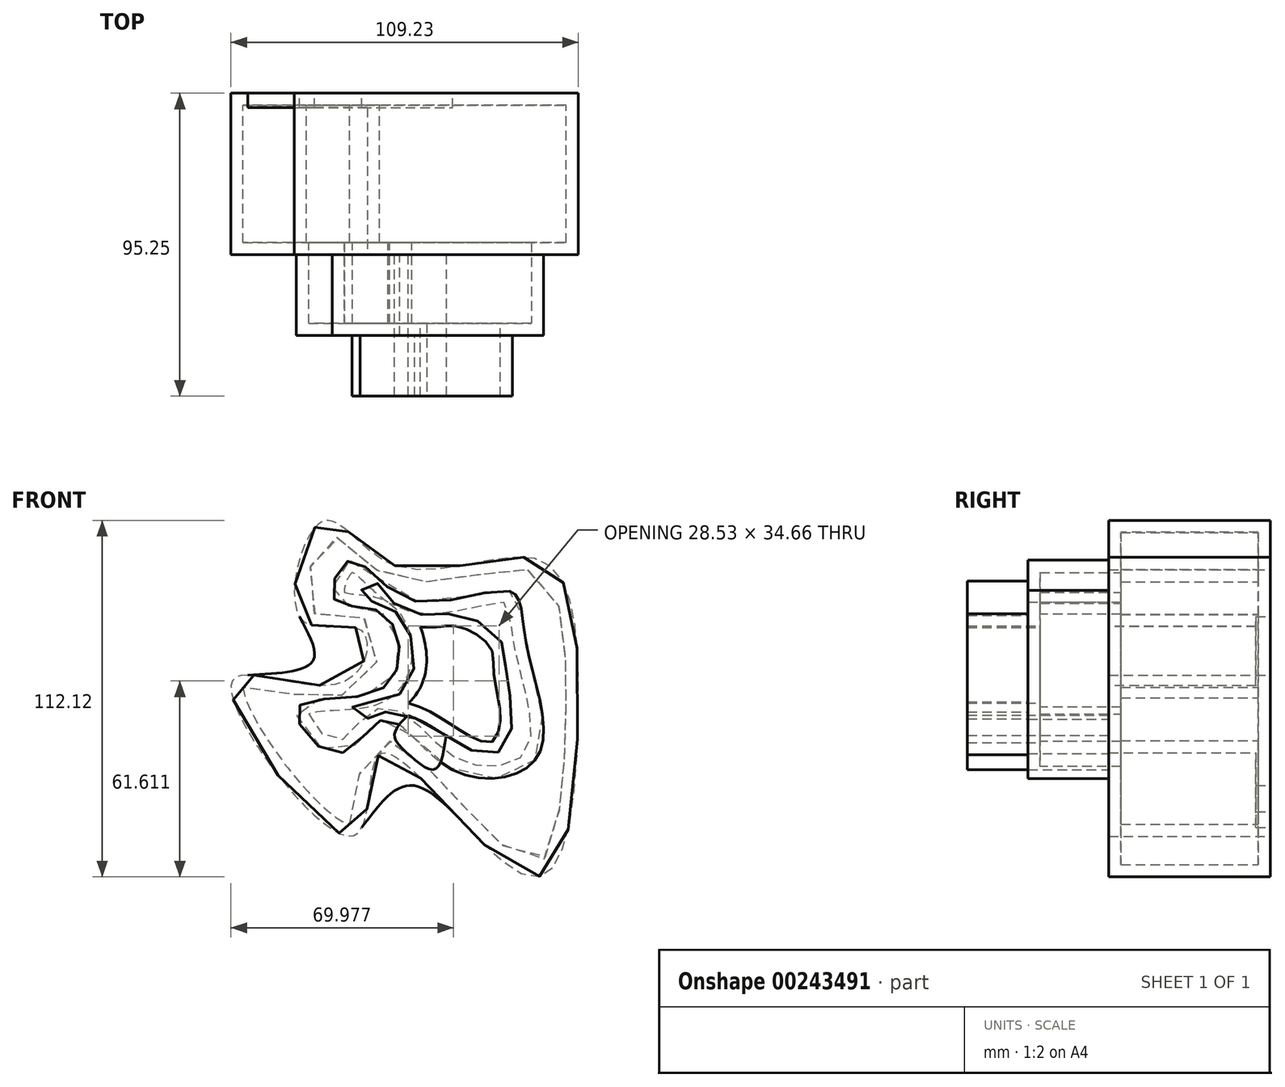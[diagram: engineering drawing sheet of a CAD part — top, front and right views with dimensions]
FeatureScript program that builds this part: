
annotation { "Feature Type Name" : "Feature", "Feature Type Description" : "" }
export const myFeature = defineFeature(function(context is Context, id is Id, definition is map)
    precondition{}
    {
        {
            var Q0;
            Q0=qCreatedBy(makeId("Front.planeOp"),FACE);
            var sketch = newSketch(context, id + "F0", { "sketchPlane" : qUnion([Q0])});
            skFitSpline(sketch, "E0", {"points": [v(-12.4, 45.2) * mm, v(-35.36, 59.05) * mm, v(-41.92, 28.43) * mm, v(-22.97, 24.79) * mm, v(-29.16, 8.38) * mm, v(-63.8, 8.38) * mm, v(-25.52, -39.73) * mm, v(-16.77, -13.85) * mm, v(29.9, -52.5) * mm, v(45.2, 0) * mm, v(32.8, 47.02) * mm, v(-12.4, 45.2) * mm]});
            skSolve(sketch);
        }
        {
            var Q0;
            Q0=makeQuery(id+"F0.imprint","IMPRINT",FACE,{"disambiguationData":[TD([[makeQuery(id+"F0.imprint","IMPRINT",EDGE,{"derivedFrom":sQuery(id+"F0.wireOp",EDGE,"E0")}),1.0]])]});
            extrude(context, id + "F1", {"entities" : qUnion([Q0]), "depth" : 50.8 * mm});
        }
        {
            var Q0;
            Q0=makeQuery(id+"F1.opExtrude","CAP_FACE",FACE,{"disambiguationData":[OSD([sQuery(id+"F0.wireOp",EDGE,"E0")])],"isStart":false});
            var sketch = newSketch(context, id + "F2", { "sketchPlane" : qUnion([Q0])});
            skFitSpline(sketch, "E1", {"points": [v(23.64, 37.21) * mm, v(-7.87, 34.52) * mm, v(-26.7, 46.82) * mm, v(-31.7, 34.9) * mm, v(-17.86, 31.06) * mm, v(-10.94, 17.61) * mm, v(-19.78, 4.93) * mm, v(-43.22, 0) * mm, v(-30.54, -13.9) * mm, v(-15.94, -3.14) * mm, v(5.58, -18.9) * mm, v(32.48, -14.67) * mm, v(28.64, 21.84) * mm, v(23.64, 37.21) * mm]});
            skSolve(sketch);
        }
        {
            var Q0;
            Q0=makeQuery(id+"F2.imprint","IMPRINT",FACE,{"disambiguationData":[TD([[makeQuery(id+"F2.imprint","IMPRINT",EDGE,{"derivedFrom":sQuery(id+"F2.wireOp",EDGE,"E1")}),1.0]])]});
            extrude(context, id + "F3", {"entities" : qUnion([Q0]), "operationType" : NewBodyOperationType.ADD, "depth" : 25.4 * mm});
        }
        {
            var Q0;
            Q0=makeQuery(id+"F3.opExtrude","CAP_FACE",FACE,{"disambiguationData":[OSD([sQuery(id+"F2.wireOp",EDGE,"E1")])],"isStart":false});
            var sketch = newSketch(context, id + "F4", { "sketchPlane" : qUnion([Q0])});
            skFitSpline(sketch, "E2", {"points": [v(21.07, 21.18) * mm, v(8.2, 29.82) * mm, v(-2.99, 29.65) * mm, v(-14.68, 35.24) * mm, v(-19.6, 40.33) * mm, v(-23.32, 35.92) * mm, v(-16.71, 33.2) * mm, v(-8.92, 26.6) * mm, v(-6.89, 11) * mm, v(-16.04, 2.54) * mm, v(-25.86, 1.52) * mm, v(-21.97, -2.89) * mm, v(-18.75, -1.36) * mm, v(-7.05, -2.38) * mm, v(6.67, -10.17) * mm, v(19.21, -13.9) * mm, v(24.46, -3.73) * mm, v(22.43, 11.86) * mm, v(21.07, 21.18) * mm]});
            skSolve(sketch);
        }
        {
            var Q0;
            Q0=makeQuery(id+"F4.imprint","IMPRINT",FACE,{"disambiguationData":[TD([[makeQuery(id+"F4.imprint","IMPRINT",EDGE,{"derivedFrom":sQuery(id+"F4.wireOp",EDGE,"E2")}),1.0]])]});
            extrude(context, id + "F5", {"entities" : qUnion([Q0]), "operationType" : NewBodyOperationType.ADD, "depth" : 19.05 * mm});
        }
        {
            var Q0;
            Q0=makeQuery(id+"F5.opExtrude","CAP_FACE",FACE,{"disambiguationData":[OSD([sQuery(id+"F4.wireOp",EDGE,"E2")])],"isStart":false});
            var sketch = newSketch(context, id + "F6", { "sketchPlane" : qUnion([Q0])});
            skFitSpline(sketch, "E3", {"points": [v(3.65, -8.28) * mm, v(0, -18.85) * mm, v(-8, -14.24) * mm, v(-12.61, -8.1) * mm, v(-8.38, -1.93) * mm], "startDerivative": vector(-7.72, -52.55) * mm, "endDerivative": vector(27.43, 27.11) * mm});
            skSolve(sketch);
        }
        {
            var Q0;
            {var subQ0=sQuery(id+"F6.wireOp",EDGE,"E3");Q0=makeQuery(id+"F6.imprint","IMPRINT",FACE,{"disambiguationData":[TD([[makeQuery(id+"F6.imprint","IMPRINT",EDGE,{"derivedFrom":subQ0}),-1.0]])]});}
            var Q1;
            Q1=makeQuery(id+"F1.opExtrude","CAP_FACE",FACE,{"disambiguationData":[OSD([sQuery(id+"F0.wireOp",EDGE,"E0")])],"isStart":false});
            extrude(context, id + "F7", {"entities" : qUnion([Q0]), "endBound" : BoundingType.UP_TO_SURFACE, "oppositeDirection" : true, "endBoundEntityFace" : qUnion([Q1]), "depth" : 25.4 * mm});
        }
        {
            var Q0;
            Q0=makeQuery(id+"F1.opExtrude","CAP_FACE",FACE,{"disambiguationData":[OSD([sQuery(id+"F0.wireOp",EDGE,"E0")])],"isStart":true});
            var sketch = newSketch(context, id + "F8", { "sketchPlane" : qUnion([Q0])});
            skFitSpline(sketch, "E4", {"points": [v(-10.72, -37.6) * mm, v(7.87, -23.9) * mm, v(22.86, -37.18) * mm], "startDerivative": vector(37.16, 40.44) * mm, "endDerivative": vector(29.9, -40.6) * mm});
            skFitSpline(sketch, "E5", {"points": [v(60.01, 10.76) * mm, v(44, 12.23) * mm, v(37.84, 16.07) * mm, v(42.85, 29.9) * mm], "startDerivative": vector(-45.3, 1.78) * mm, "endDerivative": vector(24.25, 44.34) * mm});
            skSolve(sketch);
        }
        {
            var Q0;
            {var subQ1=makeQuery(id+"F1.opExtrude","CAP_EDGE",EDGE,{"disambiguationData":[OSD([sQuery(id+"F0.wireOp",EDGE,"E0")])],"isStart":true});var subQ4=sQuery(id+"F8.wireOp",EDGE,"E4");var subQ9=makeQuery(id+"F8.imprint","INTERSECT",VERTEX,{"disambiguationData":[OD(3.0)],"derivedFrom":[subQ1,subQ4]});Q0=makeQuery(id+"F8.imprint","IMPRINT",FACE,{"disambiguationData":[TD([[makeQuery(id+"F8.imprint","IMPRINT",EDGE,{"disambiguationData":[TD([[subQ9,1.0]])],"derivedFrom":subQ4}),1.0]])]});}
            var Q1;
            {var subQ0=sQuery(id+"F8.wireOp",EDGE,"E5");var subQ1=makeQuery(id+"F1.opExtrude","CAP_EDGE",EDGE,{"disambiguationData":[OSD([sQuery(id+"F0.wireOp",EDGE,"E0")])],"isStart":true});var subQ2=makeQuery(id+"F8.imprint","INTERSECT",VERTEX,{"disambiguationData":[OD(2.0)],"derivedFrom":[subQ1,subQ0]});Q1=makeQuery(id+"F8.imprint","IMPRINT",FACE,{"disambiguationData":[TD([[makeQuery(id+"F8.imprint","IMPRINT",EDGE,{"disambiguationData":[TD([[subQ2,-1.0]])],"derivedFrom":subQ0}),1.0]])]});}
            var Q2;
            {var subQ0=sQuery(id+"F8.wireOp",EDGE,"E4");var subQ1=makeQuery(id+"F1.opExtrude","CAP_EDGE",EDGE,{"disambiguationData":[OSD([sQuery(id+"F0.wireOp",EDGE,"E0")])],"isStart":true});var subQ2=makeQuery(id+"F8.imprint","INTERSECT",VERTEX,{"disambiguationData":[OD(2.0)],"derivedFrom":[subQ1,subQ0]});Q2=makeQuery(id+"F8.imprint","IMPRINT",FACE,{"disambiguationData":[TD([[makeQuery(id+"F8.imprint","IMPRINT",EDGE,{"disambiguationData":[TD([[subQ2,1.0]])],"derivedFrom":subQ0}),1.0]])]});}
            extrude(context, id + "F9", {"entities" : qUnion([Q0, Q1, Q2]), "operationType" : NewBodyOperationType.ADD, "oppositeDirection" : true, "depth" : 4.57 * mm});
        }
        {
            var Q0;
            Q0=makeQuery(id+"F5.opExtrude","CAP_FACE",FACE,{"disambiguationData":[OSD([sQuery(id+"F4.wireOp",EDGE,"E2")])],"isStart":false});
            shell(context, id + "F10", {"entities" : qUnion([Q0]), "thickness" : 3.8 * mm});
        }
    });
